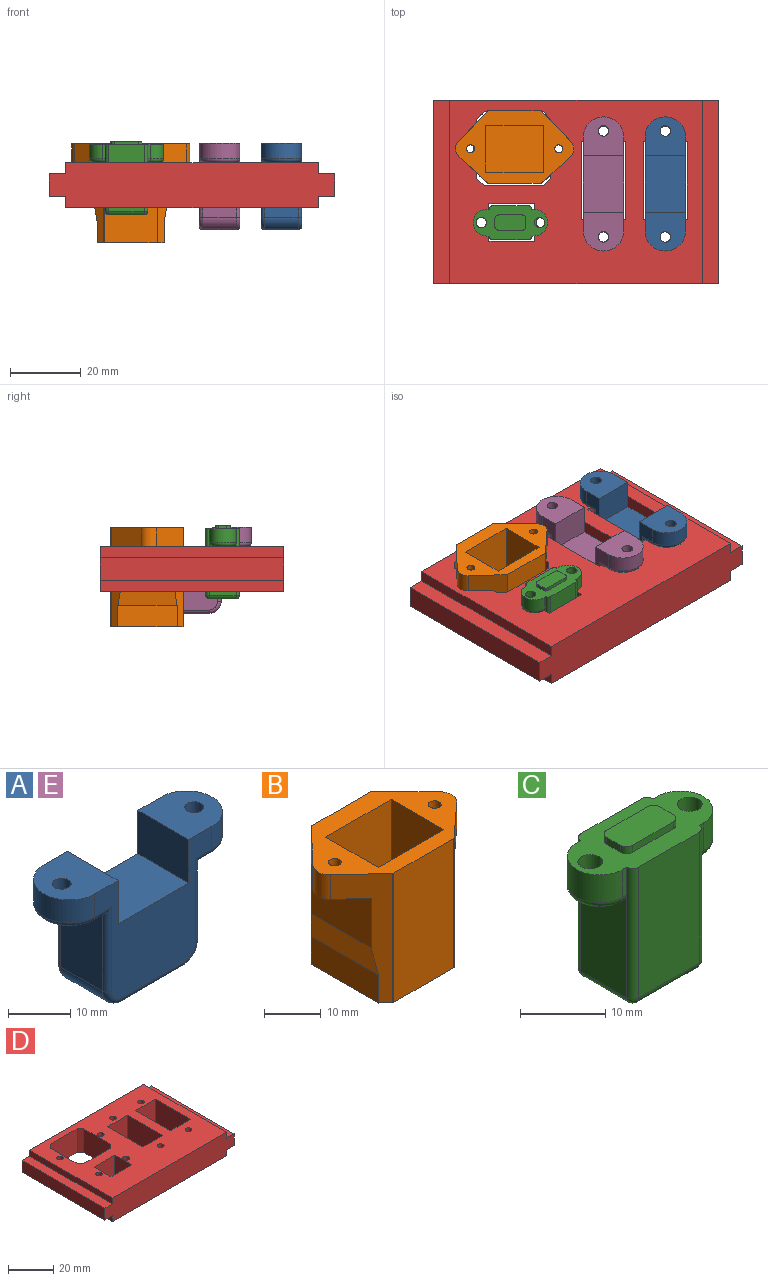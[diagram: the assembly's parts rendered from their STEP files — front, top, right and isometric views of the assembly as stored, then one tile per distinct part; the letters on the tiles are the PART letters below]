
ASSEMBLY  parts=5 mates=4
PART A: 34 faces, bbox 38.9x12.4x24.8 mm
  f0: plane 26.5x23.5mm, normal (0,1,0), area 341.5mm2, adj f1,f3,f4,f8,f9,f10,f17,f18
  f1: plane 11.5x8.5mm, normal (-1,0,0), area 97.8mm2, adj f0,f2,f4,f17
  f2: plane 26.5x23.5mm, normal (0,-1,0), area 341.5mm2, adj f1,f3,f4,f8,f9,f10,f17,f25
  f3: cylinder r=5.75mm len=11.5mm, axis (0,0,-1), area 81.3mm2, adj f0,f2,f4,f28
  f4: plane 11.5x11mm, normal (0,0,1), area 105.2mm2, adj f0,f1,f2,f3,f6
  f5: plane 9.5x7.5mm, normal (0,0,-1), area 54.5mm2, adj f6,f16,f26,f28,f30
  f6: cylinder r=1.5mm len=5.5mm, axis (0,0,-1), area 51.8mm2, adj f4,f5
  f7: plane 9.5x7.5mm, normal (0,0,-1), area 54.5mm2, adj f11,f12,f21,f23,f25
  f8: cylinder r=5.75mm len=11.5mm, axis (0,0,-1), area 81.3mm2, adj f0,f2,f10,f23
  f9: plane 11.5x8.5mm, normal (1,0,0), area 97.8mm2, adj f0,f2,f10,f17
  f10: plane 11.5x11mm, normal (0,0,1), area 105.2mm2, adj f0,f2,f8,f9,f11
  f11: cylinder r=1.5mm len=5.5mm, axis (0,0,-1), area 51.8mm2, adj f7,f10
  f12: plane 15.45x9.5mm, normal (-1,0,0), area 146.7mm2, adj f7,f13,f19,f27
  f13: cylinder r=3.57mm len=9.5mm, axis (0,1,0), area 50.2mm2, adj f12,f14,f18,f29
  f14: plane 14.49x9.5mm, normal (0,0,-1), area 137.7mm2, adj f13,f15,f20,f31
  f15: cylinder r=3.57mm len=9.5mm, axis (0,1,0), area 50.2mm2, adj f14,f16,f22,f33
  f16: plane 15.45x9.5mm, normal (1,0,0), area 146.7mm2, adj f5,f15,f24,f32
  f17: plane 16x11.5mm, normal (0,0,1), area 184mm2, adj f0,f1,f2,f9
  f18: torus R=2.57mm, axis (0,1,0), area 7.4mm2, adj f0,f13,f19,f20
  f19: cylinder r=1mm len=16.45mm, axis (0,0,-1), area 24.8mm2, adj f0,f12,f18,f21
  f20: cylinder r=1mm len=14.49mm, axis (1,0,0), area 22.7mm2, adj f0,f14,f18,f22
  f21: cylinder r=1mm len=3.75mm, axis (-1,0,0), area 4.9mm2, adj f0,f7,f19,f23
  f22: torus R=2.57mm, axis (0,1,0), area 7.4mm2, adj f0,f15,f20,f24
  f23: torus R=4.75mm, axis (0,0,1), area 26.6mm2, adj f7,f8,f21,f25
  f24: cylinder r=1mm len=16.45mm, axis (0,0,1), area 24.8mm2, adj f0,f16,f22,f26
  f25: cylinder r=1mm len=3.75mm, axis (1,0,0), area 4.9mm2, adj f2,f7,f23,f27
  f26: cylinder r=1mm len=3.75mm, axis (-1,0,0), area 4.9mm2, adj f0,f5,f24,f28
  f27: cylinder r=1mm len=16.45mm, axis (0,0,1), area 24.8mm2, adj f2,f12,f25,f29
  f28: torus R=4.75mm, axis (0,0,1), area 26.6mm2, adj f3,f5,f26,f30
  f29: torus R=2.57mm, axis (0,1,0), area 7.4mm2, adj f2,f13,f27,f31
  f30: cylinder r=1mm len=3.75mm, axis (1,0,0), area 4.9mm2, adj f2,f5,f28,f32
  f31: cylinder r=1mm len=14.49mm, axis (-1,0,0), area 22.7mm2, adj f2,f14,f29,f33
  f32: cylinder r=1mm len=16.45mm, axis (0,0,-1), area 24.8mm2, adj f2,f16,f30,f33
  f33: torus R=2.57mm, axis (0,1,0), area 7.4mm2, adj f2,f15,f31,f32
PART B: 29 faces, bbox 33.5x20.5x28 mm
  f0: cylinder r=1.13mm len=5.3mm, axis (0,0,1), area 37.6mm2, adj f19,f20
  f1: cylinder r=1.13mm len=5.3mm, axis (0,0,1), area 37.6mm2, adj f7,f20
  f2: cylinder r=3mm len=5.3mm, axis (0,0,1), area 25.3mm2, adj f15,f16,f19,f20
  f3: plane 18x13.18mm, normal (1,0,0), area 237.3mm2, adj f4,f6,f20,f24
  f4: plane 18x16.41mm, normal (0,-1,0), area 295.4mm2, adj f3,f5,f20,f24
  f5: plane 18x13.18mm, normal (-1,0,0), area 237.3mm2, adj f4,f6,f20,f24
  f6: plane 18x16.41mm, normal (0,1,0), area 295.4mm2, adj f3,f5,f20,f24
  f7: plane 14.81x6.25mm, normal (0,0,-1), area 49.7mm2, adj f1,f9,f10,f11,f21
  f8: cylinder r=0.25mm len=28mm, axis (0,0,1), area 5.7mm2, adj f9,f18,f20,f23
  f9: plane 28x8.62mm, normal (0.72,0.69,0), area 142.8mm2, adj f7,f8,f10,f20,f21,f23,f25,f26
  f10: cylinder r=3mm len=5.3mm, axis (0,0,1), area 25.3mm2, adj f7,f9,f11,f20
  f11: plane 28x8.11mm, normal (0.68,-0.74,0), area 133.4mm2, adj f7,f10,f12,f20,f21,f23,f25,f26
  f12: cylinder r=0.25mm len=28mm, axis (0,0,1), area 5.2mm2, adj f11,f13,f20,f23
  f13: plane 28x15mm, normal (0,-1,0), area 420mm2, adj f12,f14,f20,f23
  f14: cylinder r=0.25mm len=28mm, axis (0,0,1), area 5.2mm2, adj f13,f15,f20,f23
  f15: plane 28x8.11mm, normal (-0.68,-0.74,0), area 133.4mm2, adj f2,f14,f19,f20,f22,f23,f27,f28
  f16: plane 28x8.62mm, normal (-0.72,0.69,0), area 142.8mm2, adj f2,f17,f19,f20,f22,f23,f27,f28
  f17: cylinder r=0.25mm len=28mm, axis (0,0,1), area 5.7mm2, adj f16,f18,f20,f23
  f18: plane 28x15mm, normal (0,1,0), area 420mm2, adj f8,f17,f20,f23
  f19: plane 14.81x6.25mm, normal (0,0,-1), area 49.7mm2, adj f0,f2,f15,f16,f22
  f20: plane 33.5x20.5mm, normal (0,0,1), area 297.1mm2, adj f0,f1,f2,f3,f4,f5,f6,f8
  f21: plane 14.81x10.7mm, normal (1,0,0), area 158.4mm2, adj f7,f9,f11,f26
  f22: plane 14.81x10.7mm, normal (-1,0,0), area 158.4mm2, adj f15,f16,f19,f27
  f23: plane 20.5x19mm, normal (0,0,-1), area 382.4mm2, adj f8,f9,f11,f12,f13,f14,f15,f16
  f24: plane 16.41x13.18mm, normal (0,0,1), area 216.3mm2, adj f3,f4,f5,f6
  f25: plane 16.77x6mm, normal (1,0,0), area 100.6mm2, adj f9,f11,f23,f26
  f26: plane 16.77x6mm, normal (0.99,0,-0.16), area 96mm2, adj f9,f11,f21,f25
  f27: plane 16.77x6mm, normal (-0.99,0,-0.16), area 96mm2, adj f15,f16,f22,f28
  f28: plane 16.77x6mm, normal (-1,0,0), area 100.6mm2, adj f15,f16,f23,f27
PART C: 43 faces, bbox 21.6x9.6x20.8 mm
  f0: plane 21x9.6mm, normal (0,0,1), area 120.2mm2, adj f1,f2,f4,f5,f6,f7,f10,f12
  f1: plane 4x0.7mm, normal (0,-1,0), area 2.8mm2, adj f0,f4,f21,f31
  f2: plane 4x0.7mm, normal (0,1,0), area 2.8mm2, adj f0,f4,f23,f33
  f3: plane 5.6x3.33mm, normal (0,0,-1), area 9.9mm2, adj f9,f20,f21,f22,f23
  f4: cylinder r=3.8mm len=7.6mm, axis (0,0,1), area 47.8mm2, adj f0,f1,f2,f22
  f5: plane 4x0.7mm, normal (0,-1,0), area 2.8mm2, adj f0,f6,f24,f36
  f6: cylinder r=3.8mm len=7.6mm, axis (0,0,1), area 47.8mm2, adj f0,f5,f7,f25
  f7: plane 4x0.7mm, normal (0,1,0), area 2.8mm2, adj f0,f6,f26,f42
  f8: plane 5.6x3.33mm, normal (0,0,-1), area 9.9mm2, adj f11,f19,f24,f25,f26
  f9: plane 14.8x7.6mm, normal (-1,0,0), area 105.3mm2, adj f3,f21,f23,f31,f33,f34
  f10: plane 18.8x10mm, normal (0,-1,0), area 188mm2, adj f0,f31,f35,f36
  f11: plane 14.8x7.6mm, normal (1,0,0), area 105.3mm2, adj f8,f24,f26,f36,f40,f42
  f12: plane 18.8x10mm, normal (0,1,0), area 188mm2, adj f0,f33,f39,f42
  f13: plane 10x7.6mm, normal (0,0,-1), area 76mm2, adj f34,f35,f39,f40
  f14: plane 6.8x1mm, normal (0,-1,0), area 6.8mm2, adj f0,f18,f27,f30
  f15: plane 2.3x1mm, normal (1,0,0), area 2.3mm2, adj f0,f18,f27,f28
  f16: plane 6.8x1mm, normal (0,1,0), area 6.8mm2, adj f0,f18,f28,f29
  f17: plane 2.3x1mm, normal (-1,0,0), area 2.3mm2, adj f0,f18,f29,f30
  f18: plane 8.8x4.3mm, normal (0,0,1), area 37mm2, adj f14,f15,f16,f17,f27,f28,f29,f30
  f19: cylinder r=1.45mm len=5mm, axis (0,0,1), area 45.5mm2, adj f0,f8,f25
  f20: cylinder r=1.45mm len=5mm, axis (0,0,1), area 45.5mm2, adj f0,f3,f22
  f21: cylinder r=1mm len=1mm, axis (-1,0,0), area 1.1mm2, adj f1,f3,f9,f22
  f22: torus R=2.8mm, axis (0,0,1), area 16.7mm2, adj f3,f4,f20,f21,f23
  f23: cylinder r=1mm len=1mm, axis (1,0,0), area 1.1mm2, adj f2,f3,f9,f22
  f24: cylinder r=1mm len=1mm, axis (-1,0,0), area 1.1mm2, adj f5,f8,f11,f25
  f25: torus R=2.8mm, axis (0,0,1), area 16.7mm2, adj f6,f8,f19,f24,f26
  f26: cylinder r=1mm len=1mm, axis (1,0,0), area 1.1mm2, adj f7,f8,f11,f25
  f27: cylinder r=1mm len=1mm, axis (0,0,1), area 1.6mm2, adj f0,f14,f15,f18
  f28: cylinder r=1mm len=1mm, axis (0,0,-1), area 1.6mm2, adj f0,f15,f16,f18
  f29: cylinder r=1mm len=1mm, axis (0,0,1), area 1.6mm2, adj f0,f16,f17,f18
  f30: cylinder r=1mm len=1mm, axis (0,0,-1), area 1.6mm2, adj f0,f14,f17,f18
  f31: cylinder r=1mm len=18.8mm, axis (0,0,1), area 29.5mm2, adj f0,f1,f9,f10,f32
  f32: sphere r=1mm, area 1.6mm2, adj f31,f34,f35
  f33: cylinder r=1mm len=18.8mm, axis (0,0,-1), area 29.5mm2, adj f0,f2,f9,f12,f37
  f34: cylinder r=1mm len=7.6mm, axis (0,1,0), area 11.9mm2, adj f9,f13,f32,f37
  f35: cylinder r=1mm len=10mm, axis (-1,0,0), area 15.7mm2, adj f10,f13,f32,f38
  f36: cylinder r=1mm len=18.8mm, axis (0,0,-1), area 29.5mm2, adj f0,f5,f10,f11,f38
  f37: sphere r=1mm, area 1.6mm2, adj f33,f34,f39
  f38: sphere r=1mm, area 1.6mm2, adj f35,f36,f40
  f39: cylinder r=1mm len=10mm, axis (1,0,0), area 15.7mm2, adj f12,f13,f37,f41
  f40: cylinder r=1mm len=7.6mm, axis (0,-1,0), area 11.9mm2, adj f11,f13,f38,f41
  f41: sphere r=1mm, area 1.6mm2, adj f39,f40,f42
  f42: cylinder r=1mm len=18.8mm, axis (0,0,1), area 29.5mm2, adj f0,f7,f11,f12,f41
PART D: 42 faces, bbox 81x52x12.8 mm
  f0: plane 71.6x52mm, normal (0,0,1), area 2550.5mm2, adj f4,f5,f6,f7,f14,f15,f16,f17
  f1: plane 71.6x52mm, normal (0,0,-1), area 2550.5mm2, adj f2,f3,f4,f6,f14,f15,f16,f17
  f2: plane 52x3.2mm, normal (1,0,0), area 166.4mm2, adj f1,f4,f6,f13
  f3: plane 52x3.2mm, normal (-1,0,0), area 166.4mm2, adj f1,f4,f6,f10
  f4: plane 81x12.8mm, normal (0,1,0), area 976.6mm2, adj f0,f1,f2,f3,f5,f7,f8,f9
  f5: plane 52x3.2mm, normal (-1,0,0), area 166.4mm2, adj f0,f4,f6,f9
  f6: plane 81x12.8mm, normal (0,-1,0), area 976.6mm2, adj f0,f1,f2,f3,f5,f7,f8,f9
  f7: plane 52x3.2mm, normal (1,0,0), area 166.4mm2, adj f0,f4,f6,f12
  f8: plane 52x6.4mm, normal (-1,0,0), area 332.8mm2, adj f4,f6,f9,f10
  f9: plane 52x4.7mm, normal (0,0,1), area 244.4mm2, adj f4,f5,f6,f8
  f10: plane 52x4.7mm, normal (0,0,-1), area 244.4mm2, adj f3,f4,f6,f8
  f11: plane 52x6.4mm, normal (1,0,0), area 332.8mm2, adj f4,f6,f12,f13
  f12: plane 52x4.7mm, normal (0,0,1), area 244.4mm2, adj f4,f6,f7,f11
  f13: plane 52x4.7mm, normal (0,0,-1), area 244.4mm2, adj f2,f4,f6,f11
  f14: plane 12.8x2.11mm, normal (0.71,0.71,0), area 38.3mm2, adj f0,f1,f15,f21
  f15: plane 16.77x12.8mm, normal (0,1,0), area 214.7mm2, adj f0,f1,f14,f16
  f16: plane 12.8x2.11mm, normal (-0.71,0.71,0), area 38.3mm2, adj f0,f1,f15,f17
  f17: plane 16.77x12.8mm, normal (-1,0,0), area 214.7mm2, adj f0,f1,f16,f18
  f18: plane 12.8x2.11mm, normal (-0.71,-0.71,0), area 38.3mm2, adj f0,f1,f17,f19
  f19: plane 16.77x12.8mm, normal (0,-1,0), area 214.7mm2, adj f0,f1,f18,f20
  f20: plane 12.8x2.11mm, normal (0.71,-0.71,0), area 38.3mm2, adj f0,f1,f19,f21
  f21: plane 16.77x12.8mm, normal (1,0,0), area 214.7mm2, adj f0,f1,f14,f20
  f22: plane 12.8x12.5mm, normal (0,-1,0), area 160mm2, adj f0,f1,f23,f24
  f23: plane 22x12.8mm, normal (-1,0,0), area 281.6mm2, adj f0,f1,f22,f25
  f24: plane 22x12.8mm, normal (1,0,0), area 281.6mm2, adj f0,f1,f22,f25
  f25: plane 12.8x12.5mm, normal (0,1,0), area 160mm2, adj f0,f1,f23,f24
  f26: plane 12.8x12.5mm, normal (0,1,0), area 160mm2, adj f0,f1,f27,f29
  f27: plane 22x12.8mm, normal (-1,0,0), area 281.6mm2, adj f0,f1,f26,f28
  f28: plane 12.8x12.5mm, normal (0,-1,0), area 160mm2, adj f0,f1,f27,f29
  f29: plane 22x12.8mm, normal (1,0,0), area 281.6mm2, adj f0,f1,f26,f28
  f30: plane 12.8x10.6mm, normal (-1,0,0), area 135.7mm2, adj f0,f1,f31,f32
  f31: plane 13x12.8mm, normal (0,1,0), area 166.4mm2, adj f0,f1,f30,f33
  f32: plane 13x12.8mm, normal (0,-1,0), area 166.4mm2, adj f0,f1,f30,f33
  f33: plane 12.8x10.6mm, normal (1,0,0), area 135.7mm2, adj f0,f1,f31,f32
  f34: cylinder r=1.45mm len=12.8mm, axis (0,0,1), area 116.6mm2, adj f0,f1
  f35: cylinder r=1.45mm len=12.8mm, axis (0,0,1), area 116.6mm2, adj f0,f1
  f36: cylinder r=1.45mm len=12.8mm, axis (0,0,1), area 116.6mm2, adj f0,f1
  f37: cylinder r=1.45mm len=12.8mm, axis (0,0,1), area 116.6mm2, adj f0,f1
  f38: cylinder r=1.45mm len=12.8mm, axis (0,0,1), area 116.6mm2, adj f0,f1
  f39: cylinder r=1.45mm len=12.8mm, axis (0,0,1), area 116.6mm2, adj f0,f1
  f40: cylinder r=1.45mm len=12.8mm, axis (0,0,1), area 116.6mm2, adj f0,f1
  f41: cylinder r=1.45mm len=12.8mm, axis (0,0,1), area 116.6mm2, adj f0,f1
PART E: same geometry as A
PLACE A rot(axis=(0,0,1),90deg) t=(61.45,27.77,3.21)mm
PLACE B t=(18.78,37.72,8.51)mm
PLACE C t=(17.58,16.83,8.21)mm
PLACE D t=(-4.12,-0.29,-3.19)mm fixed
PLACE E rot(axis=(0,0,1),90deg) t=(43.95,27.77,3.21)mm
MATE fastened C.f20 <-> D.f39  axis (0,0,-1) through (9.33,16.83,3.21)mm
MATE fastened B.f1 <-> D.f37  axis (0,0,1) through (31.28,37.72,3.21)mm
MATE fastened A.f6 <-> D.f34  axis (0,0,-1) through (61.45,42.77,3.21)mm
MATE fastened E.f6 <-> D.f36  axis (0,0,-1) through (43.95,42.77,3.21)mm
